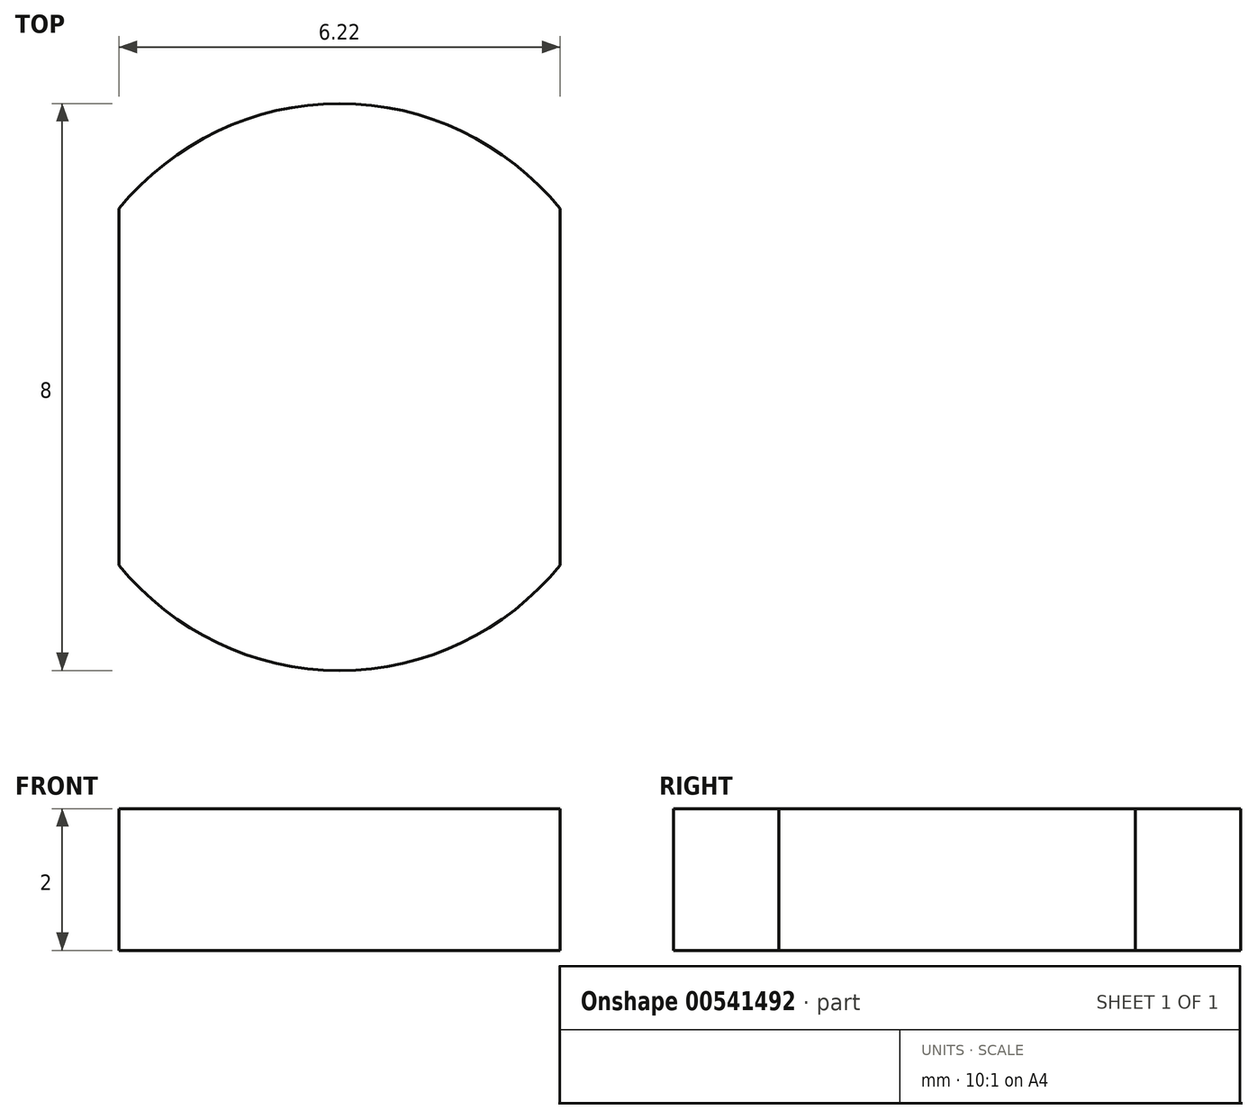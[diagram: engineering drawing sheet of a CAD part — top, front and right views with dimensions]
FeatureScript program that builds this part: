
annotation { "Feature Type Name" : "Feature", "Feature Type Description" : "" }
export const myFeature = defineFeature(function(context is Context, id is Id, definition is map)
    precondition{}
    {
        {
            var Q0;
            Q0=qCreatedBy(makeId("Top.planeOp"),FACE);
            var sketch = newSketch(context, id + "F0", { "sketchPlane" : qUnion([Q0])});
            skCircle(sketch, "E0", {"center": v(0, 0) * mm, "radius": 4 * mm});
            skSolve(sketch);
        }
        {
            var Q0;
            Q0 = qSketchRegion(id + "F0", true);
            extrude(context, id + "F1", {"entities" : qUnion([Q0]), "depth" : 2 * mm, "offsetDistance" : 25 * mm});
        }
        {
            var Q0;
            Q0=makeQuery(id+"F1.opExtrude","CAP_FACE",FACE,{"disambiguationData":[OSD([sQuery(id+"F0.wireOp",EDGE,"E0")])],"isStart":false});
            var sketch = newSketch(context, id + "F2", { "sketchPlane" : qUnion([Q0])});
            skLineSegment(sketch, "E1", {"start": v(-3.1, 2.52) * mm, "end": v(-3.1, -2.52) * mm});
            skLineSegment(sketch, "E2", {"start": v(3.1, 2.52) * mm, "end": v(3.1, -2.52) * mm});
            skArc(sketch, "E3", {"start": v(-3.1, -2.52) * mm, "mid": v(0, -4) * mm, "end": v(3.1, -2.52) * mm});
            skArc(sketch, "E4.trimOffspring", {"start": v(3.1, 2.52) * mm, "mid": v(0, 4) * mm, "end": v(-3.1, 2.52) * mm});
            skSolve(sketch);
        }
        {
            var Q0;
            {var subQ0=sQuery(id+"F2.wireOp",EDGE,"E1");Q0=makeQuery(id+"F2.imprint","IMPRINT",FACE,{"disambiguationData":[TD([[makeQuery(id+"F2.imprint","IMPRINT",EDGE,{"derivedFrom":subQ0}),-1.0]])]});}
            var Q1;
            {var subQ0=sQuery(id+"F2.wireOp",EDGE,"E2");Q1=makeQuery(id+"F2.imprint","IMPRINT",FACE,{"disambiguationData":[TD([[makeQuery(id+"F2.imprint","IMPRINT",EDGE,{"derivedFrom":subQ0}),1.0]])]});}
            extrude(context, id + "F3", {"entities" : qUnion([Q0, Q1]), "operationType" : NewBodyOperationType.REMOVE, "endBound" : BoundingType.THROUGH_ALL, "oppositeDirection" : true, "depth" : 25 * mm, "offsetDistance" : 25 * mm});
        }
    });
